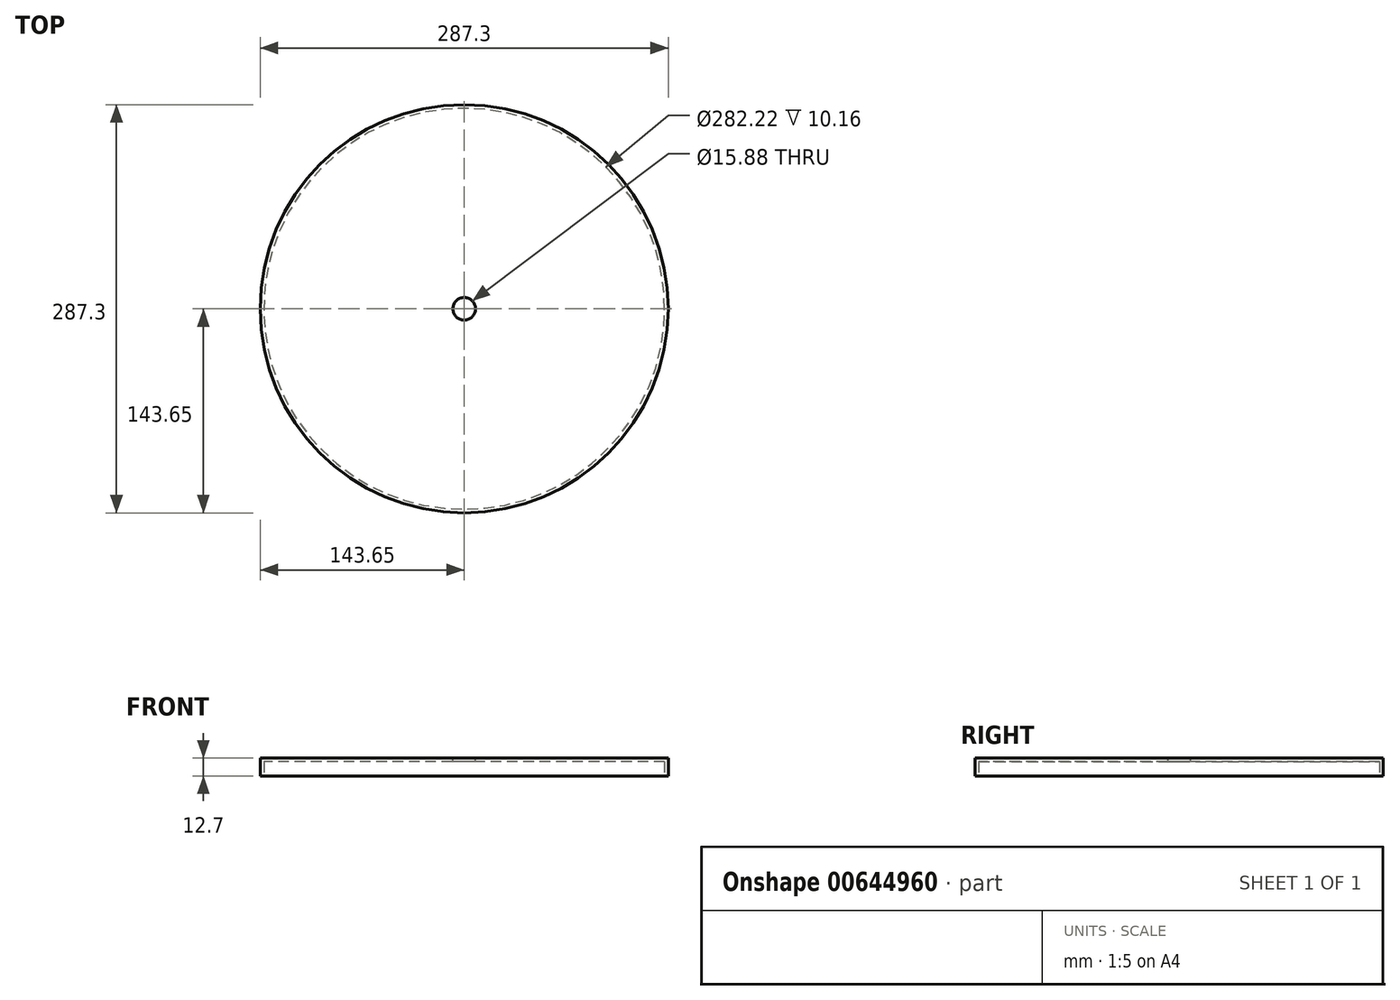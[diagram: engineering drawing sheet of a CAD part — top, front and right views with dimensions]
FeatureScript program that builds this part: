
annotation { "Feature Type Name" : "Feature", "Feature Type Description" : "" }
export const myFeature = defineFeature(function(context is Context, id is Id, definition is map)
    precondition{}
    {
        {
            var Q0;
            Q0=qCreatedBy(makeId("Top.planeOp"),FACE);
            var sketch = newSketch(context, id + "F0", { "sketchPlane" : qUnion([Q0])});
            skCircle(sketch, "E0", {"center": v(0, 0) * mm, "radius": 143.65 * mm});
            skSolve(sketch);
        }
        {
            var Q0;
            Q0 = qSketchRegion(id + "F0", true);
            extrude(context, id + "F1", {"entities" : qUnion([Q0]), "depth" : 12.7 * mm, "offsetDistance" : 25.4 * mm});
        }
        {
            var Q0;
            Q0=makeQuery(id+"F1.opExtrude","CAP_FACE",FACE,{"disambiguationData":[OSD([sQuery(id+"F0.wireOp",EDGE,"E0")])],"isStart":true});
            shell(context, id + "F2", {"entities" : qUnion([Q0]), "thickness" : 2.54 * mm});
        }
        {
            var Q0;
            Q0=makeQuery(id+"F1.opExtrude","CAP_FACE",FACE,{"disambiguationData":[OSD([sQuery(id+"F0.wireOp",EDGE,"E0")])],"isStart":false});
            var sketch = newSketch(context, id + "F3", { "sketchPlane" : qUnion([Q0])});
            skCircle(sketch, "E1", {"center": v(0, 0) * mm, "radius": 6.35 * mm});
            skSolve(sketch);
        }
        {
            var Q0;
            Q0=sQuery(id+"F3.wireOp",VERTEX,"E1.center");
            var Q1;
            Q1=makeQuery(id+"F1.opExtrude","SWEPT_BODY",BODY,{"disambiguationData":[OSD([sQuery(id+"F0.wireOp",EDGE,"E0")])]});
            hole(context, id + "F4", {"style" : HoleStyle.SIMPLE, "endStyle" : HoleEndStyle.THROUGH, "holeDiameter" : 15.88 * mm, "majorDiameter" : 6.35 * mm, "isTappedThrough" : true, "tappedDepth" : 12.7 * mm, "tapClearance" : 3, "locations" : qUnion([Q0]), "scope" : qUnion([Q1])});
        }
    });
